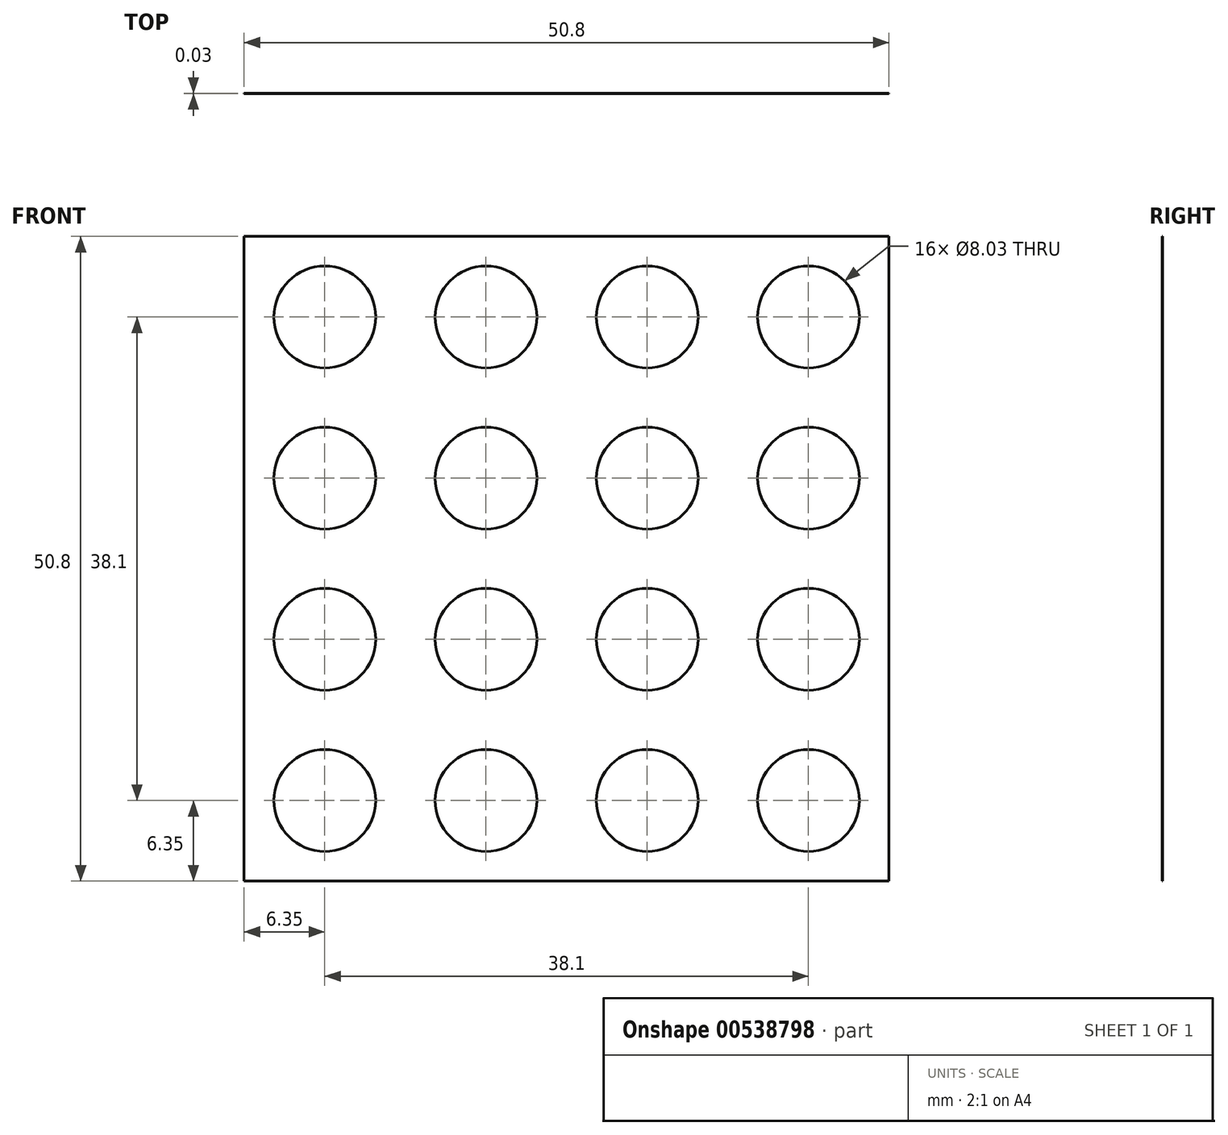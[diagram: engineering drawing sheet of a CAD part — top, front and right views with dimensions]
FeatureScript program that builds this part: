
annotation { "Feature Type Name" : "Feature", "Feature Type Description" : "" }
export const myFeature = defineFeature(function(context is Context, id is Id, definition is map)
    precondition{}
    {
        {
            var Q0;
            Q0=qCreatedBy(makeId("Front.planeOp"),FACE);
            var sketch = newSketch(context, id + "F0", { "sketchPlane" : qUnion([Q0])});
            skLineSegment(sketch, "E0", {"start": v(0, 0) * mm, "end": v(50.8, 0) * mm});
            skLineSegment(sketch, "E1", {"start": v(50.8, 0) * mm, "end": v(50.8, 50.8) * mm});
            skLineSegment(sketch, "E2", {"start": v(50.8, 50.8) * mm, "end": v(0, 50.8) * mm});
            skLineSegment(sketch, "E3", {"start": v(0, 50.8) * mm, "end": v(0, 0) * mm});
            skPoint(sketch, "E4.startSnap0", {"position": v(12.7, 12.7) * mm});
            skPoint(sketch, "E5.startSnap0", {"position": v(38.1, 38.1) * mm});
            skPoint(sketch, "E6", {"position": v(6.35, 44.45) * mm});
            skPoint(sketch, "E7", {"position": v(19.05, 44.45) * mm});
            skPoint(sketch, "E8", {"position": v(31.75, 44.45) * mm});
            skPoint(sketch, "E9", {"position": v(44.45, 44.45) * mm});
            skPoint(sketch, "E10", {"position": v(44.45, 31.75) * mm});
            skPoint(sketch, "E11", {"position": v(31.75, 31.75) * mm});
            skPoint(sketch, "E12", {"position": v(19.05, 31.75) * mm});
            skPoint(sketch, "E13", {"position": v(6.35, 31.75) * mm});
            skPoint(sketch, "E14", {"position": v(6.35, 19.05) * mm});
            skPoint(sketch, "E15", {"position": v(19.05, 19.05) * mm});
            skPoint(sketch, "E16", {"position": v(31.75, 19.05) * mm});
            skPoint(sketch, "E17", {"position": v(44.45, 19.05) * mm});
            skPoint(sketch, "E18", {"position": v(44.45, 6.35) * mm});
            skPoint(sketch, "E19", {"position": v(31.75, 6.35) * mm});
            skPoint(sketch, "E20", {"position": v(19.05, 6.35) * mm});
            skPoint(sketch, "E21", {"position": v(6.35, 6.35) * mm});
            skCircle(sketch, "E22", {"center": v(6.35, 44.45) * mm, "radius": 4.02 * mm});
            skCircle(sketch, "E23", {"center": v(19.05, 44.45) * mm, "radius": 4.01 * mm});
            skCircle(sketch, "E24", {"center": v(31.75, 44.45) * mm, "radius": 4.01 * mm});
            skCircle(sketch, "E25", {"center": v(44.45, 44.45) * mm, "radius": 4.01 * mm});
            skCircle(sketch, "E26", {"center": v(31.75, 31.75) * mm, "radius": 4.01 * mm});
            skCircle(sketch, "E27", {"center": v(44.45, 31.75) * mm, "radius": 4.01 * mm});
            skCircle(sketch, "E28", {"center": v(19.05, 31.75) * mm, "radius": 4.01 * mm});
            skCircle(sketch, "E29", {"center": v(6.35, 31.75) * mm, "radius": 4.01 * mm});
            skCircle(sketch, "E30", {"center": v(6.35, 19.05) * mm, "radius": 4.01 * mm});
            skCircle(sketch, "E31", {"center": v(19.05, 19.05) * mm, "radius": 4.01 * mm});
            skCircle(sketch, "E32", {"center": v(31.75, 19.05) * mm, "radius": 4.01 * mm});
            skCircle(sketch, "E33", {"center": v(44.45, 19.05) * mm, "radius": 4.01 * mm});
            skCircle(sketch, "E34", {"center": v(44.45, 6.35) * mm, "radius": 4.01 * mm});
            skCircle(sketch, "E35", {"center": v(31.75, 6.35) * mm, "radius": 4.01 * mm});
            skCircle(sketch, "E36", {"center": v(19.05, 6.35) * mm, "radius": 4.01 * mm});
            skCircle(sketch, "E37", {"center": v(6.35, 6.35) * mm, "radius": 4.01 * mm});
            skSolve(sketch);
        }
        {
            var Q0;
            Q0=makeQuery(id+"F0.imprint","IMPRINT",FACE,{"disambiguationData":[TD([[makeQuery(id+"F0.imprint","IMPRINT",EDGE,{"derivedFrom":sQuery(id+"F0.wireOp",EDGE,"E0")}),1.0]])]});
            extrude(context, id + "F1", {"entities" : qUnion([Q0]), "depth" : 0.03 * mm, "offsetDistance" : 25.4 * mm});
        }
    });
